# Revit family: Electronics_Loudspeaker_Bose-Professional_Designmax_DM8C-SUB
name_source: partatom
category: Communication Devices
revit_build: Autodesk Revit 2015 (Build: 20140905_0730(x64)
units: mm (PartAtom-declared; Revit-internal decimal feet)

## types (2) — shared parameters
Assembly Code = D5030
Bracket Material = Metal-Bose-Aluminium
Crossover = 80 - 200 Hz (via active crossover in DSP)
Default Elevation = 1219 mm
Depth = 255 mm
Description = Premium sound to maximize any design.
DesignMax loudspeakers bring outstanding audio and aesthetics to any commercial space. With 12 models to choose from, it’s easy to create tailored solutions that deliver instantly impressive sound. QuickHold mounting mechanisms make installation efficient, reducing strain and hassle — and saving substantial time. And with both black and white versions available, DesignMax loudspeakers integrate seamlessly with any décor.

The 150-watt DesignMax DM8C-SUB subwoofer features an 8-inch woofer, which delivers a 42 Hz - 300 Hz frequency range. The DM8C-SUB is ceiling-mounted, installed easily via QuickHold mounting arms

FEATURES
Combine models to complete any design, big or small — 12 loudspeakers to mix and match, from 2-inch, low-profile models to 8-inch, high-SPL compression-driver loudspeakers and outdoor-rated options

Deliver instantly impressive sound with custom Bose drivers — no DSP or EQ required. For even better sound, use select Bose DSPs and amplifiers to enable Bose loudspeaker EQ and SmartBass processing, which expands performance and response at any listening level

Blend into any room design with elegant form factors, minimum-bezel grilles available in black or white, and removable logos

Reduce installation time with the patented QuickHold mounting system, which also reduces strain, hassle, and the chance of product damage

Install easily — all models include Euroblock connectors; ceiling-mounted models include plenum-rated backcans, tile-bridges, and front-access audio wiring that makes installation and troubleshooting easier

Applications
Performing arts venues
Places of worship
Conference centers
Retail stores
Restaurants and bars
Hospitality venues
Diameter = 409 mm
Edition number = 1
Environmental = indoor only
Frequency Range = 42 - 300 Hz
Frequency Response = 50 - 200 Hz
Height = 0 mm
Keynote = 16700
LF Driver = 1 x 8-inch woofer (203 mm)
Manufacturer = Bose Professional
Maximum Ceiling Thickness = 76 mm
Model = DesignMax DM8C-SUB
Mounting/Suspension = Three (3) QuickHold, spring-loaded mounting arms plus three (3) safety cable locations
Nominal Coverage Pattern = Omnidirectional below 200 Hz
Nominal Impedance = 8 Ω
Nominal Sensitivity = Bose Extended Lifecycle Test: 91 dB; AES Transducer Test: Free field  91 dB
Operating Temperature Range = 0 to 50 °C (32 °F to 122 °F)
Power Connector = Euroblock 6-pin connector with loop-through, front-baffle mounted. Accepts 18 AWG (0.8 mm2) to 14 AWG (2.5 mm2) size wire.
Power Handling(Long-term continuous) = Bose Extended Lifecycle Test: 150W; AES Transducer Test: 180W
Power Handling(peak) = Bose Extended Lifecycle Test: 600W; AES Transducer Test: 720W
Product Guid = e775235c-a9b4-4977-8d69-6c860d4eb0cd
Product data url = https://www.bimobject.com
Rated Maximum SPL = Calculated max. SPL @ 1 m (Bose power test) -  113 dB ; Calculated max. SPL @ 1 m (2-hour power test) -  119 dB; Calculated max. SPL @ 1 m (Bose power test), peak -  114 dB; Calculated max. SPL @ 1 m (2-hour power test), peak - 120 dB;
Recommended High-pass Filter = 45 Hz with 24-dB / octave filter
Safety Agency = UL-1480A, S5591/ UL Listed, in compliance with UL2043 for plenum-space installation, NFPA70 & NFPA90-A, in accordance with IEC60268-5, ROHS, CE compliant
Transformer Taps Information = 70V: 2.5, 5, 10, 20, 40, 80 W, bypass, 100V: 5, 10, 20, 40, 80 W, bypass
URL = https://www.bose.com
Weight = 0.00 kg
Width = 0 mm
Wire/ Conduit Entry = Single top wire entry point, allows for 9.5 mm (3/8 “) conduit

## per-type parameters (varying)
| type | Mesh Material | Product code | Speaker Material |
| DM8C-Sub-Black | Grill-Bose-Black | 829380-0110 | Metal-Bose-Black |
| DM8C-Sub-White | Grill-Bose-White | 829380-0210 | Metal-Bose-White |

## geometry (parser evidence)
native form markers: Blend x8, Sweep x12
no freeform markers — native parametric forms only
